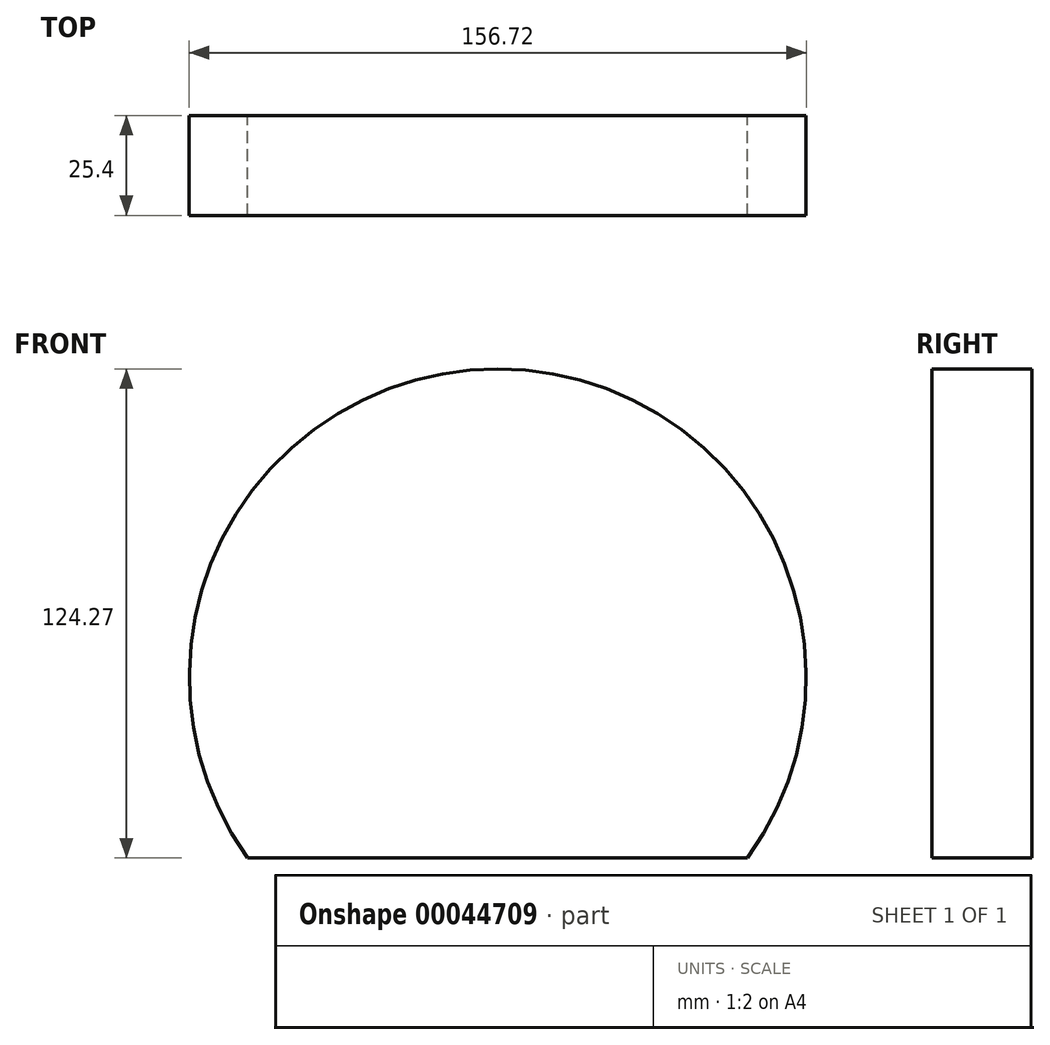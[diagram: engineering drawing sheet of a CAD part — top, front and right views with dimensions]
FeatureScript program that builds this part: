
annotation { "Feature Type Name" : "Feature", "Feature Type Description" : "" }
export const myFeature = defineFeature(function(context is Context, id is Id, definition is map)
    precondition{}
    {
        {
            var Q0;
            Q0=qCreatedBy(makeId("Front.planeOp"),FACE);
            var sketch = newSketch(context, id + "F0", { "sketchPlane" : qUnion([Q0])});
            skArc(sketch, "E0", {"start": v(63.5, -45.91) * mm, "mid": v(0, 78.36) * mm, "end": v(-63.5, -45.91) * mm});
            skLineSegment(sketch, "E1", {"start": v(-63.5, -45.91) * mm, "end": v(63.5, -45.91) * mm});
            skSolve(sketch);
        }
        {
            var Q0;
            Q0=makeQuery(id+"F0.imprint","IMPRINT",FACE,{"disambiguationData":[TD([[makeQuery(id+"F0.imprint","IMPRINT",EDGE,{"derivedFrom":sQuery(id+"F0.wireOp",EDGE,"E0")}),1.0]])]});
            extrude(context, id + "F1", {"entities" : qUnion([Q0]), "depth" : 25.4 * mm});
        }
    });
